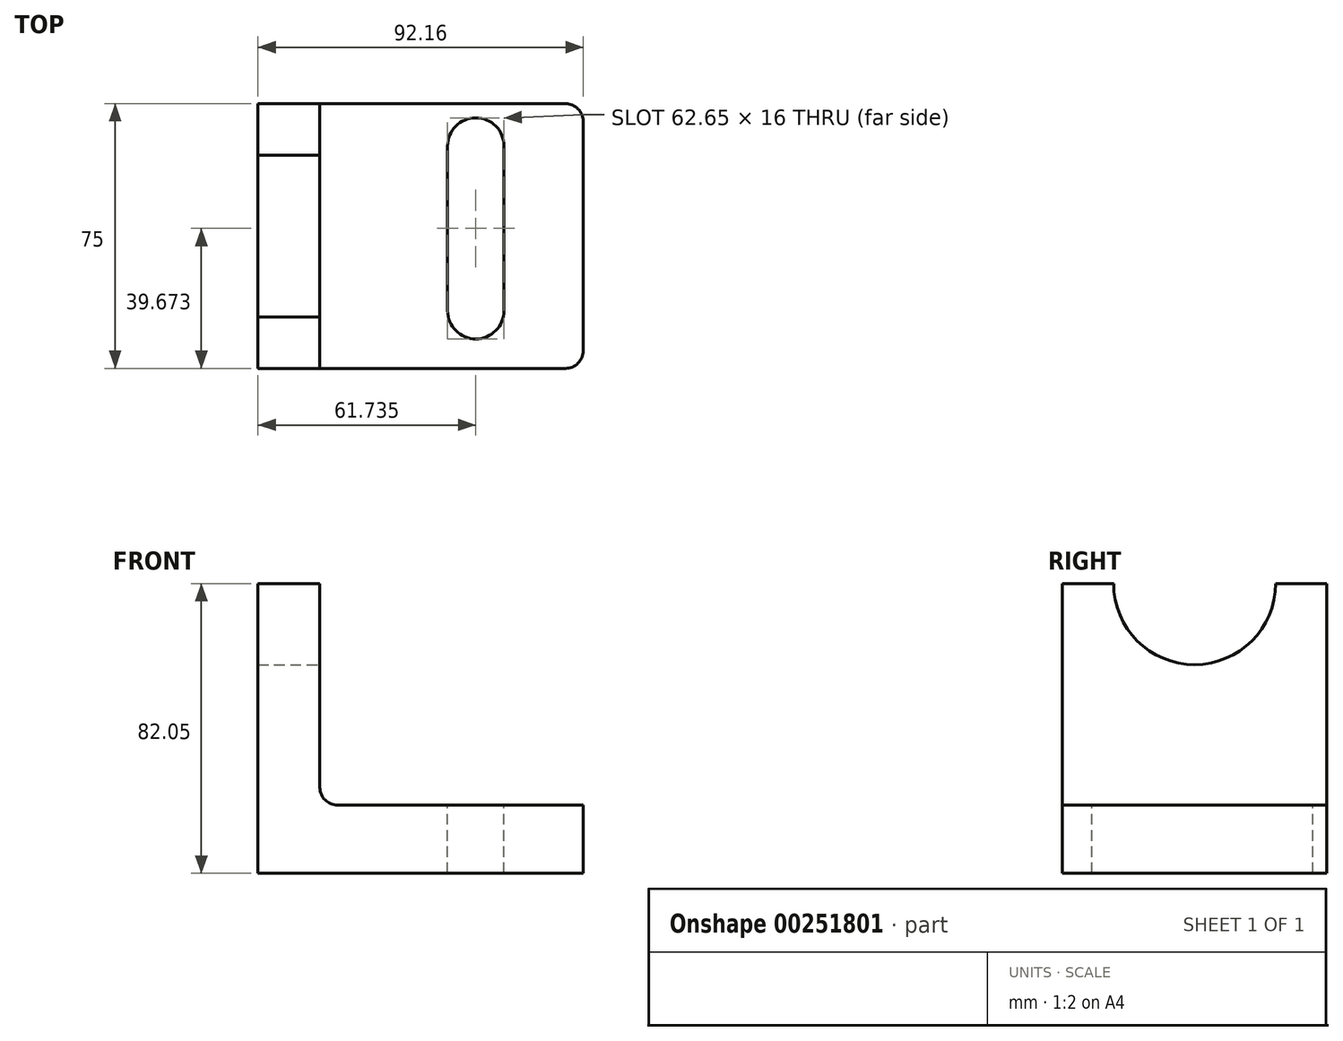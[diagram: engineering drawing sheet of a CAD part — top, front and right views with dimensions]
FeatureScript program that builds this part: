
annotation { "Feature Type Name" : "Feature", "Feature Type Description" : "" }
export const myFeature = defineFeature(function(context is Context, id is Id, definition is map)
    precondition{}
    {
        {
            var Q0;
            Q0=qCreatedBy(makeId("Front.planeOp"),FACE);
            var sketch = newSketch(context, id + "F0", { "sketchPlane" : qUnion([Q0])});
            skLineSegment(sketch, "E0.bottom", {"start": v(46.08, -9.65) * mm, "end": v(-46.08, -9.65) * mm});
            skLineSegment(sketch, "E0.top", {"start": v(46.08, 9.65) * mm, "end": v(-46.08, 9.65) * mm});
            skLineSegment(sketch, "E0.left", {"start": v(46.08, -9.65) * mm, "end": v(46.08, 9.65) * mm});
            skLineSegment(sketch, "E0.right", {"start": v(-46.08, -9.65) * mm, "end": v(-46.08, 9.65) * mm});
            skPoint(sketch, "E0.middle", {"position": v(0, 0) * mm});
            skLineSegment(sketch, "E1.bottom", {"start": v(-46.08, 9.65) * mm, "end": v(-28.52, 9.65) * mm});
            skLineSegment(sketch, "E1.top", {"start": v(-46.08, 72.4) * mm, "end": v(-28.52, 72.4) * mm});
            skLineSegment(sketch, "E1.left", {"start": v(-46.08, 9.65) * mm, "end": v(-46.08, 72.4) * mm});
            skLineSegment(sketch, "E1.right", {"start": v(-28.52, 9.65) * mm, "end": v(-28.52, 72.4) * mm});
            skSolve(sketch);
        }
        {
            var Q0;
            Q0 = qSketchRegion(id + "F0", true);
            extrude(context, id + "F1", {"entities" : qUnion([Q0]), "depth" : 75 * mm});
        }
        {
            var Q0;
            Q0=makeQuery(id+"F1.opExtrude","SWEPT_FACE",FACE,{"disambiguationData":[OSD([sQuery(id+"F0.wireOp",EDGE,"E1.right")])]});
            var sketch = newSketch(context, id + "F2", { "sketchPlane" : qUnion([Q0])});
            skCircle(sketch, "E2", {"center": v(-37.5, 72.4) * mm, "radius": 22.94 * mm});
            skSolve(sketch);
        }
        {
            var Q0;
            Q0 = qSketchRegion(id + "F2", true);
            extrude(context, id + "F3", {"entities" : qUnion([Q0]), "operationType" : NewBodyOperationType.REMOVE, "oppositeDirection" : true, "depth" : 25 * mm});
        }
        {
            var Q0;
            Q0=makeQuery(id+"F1.opExtrude","SWEPT_FACE",FACE,{"disambiguationData":[OSD([sQuery(id+"F0.wireOp",EDGE,"E0.top")])]});
            var sketch = newSketch(context, id + "F4", { "sketchPlane" : qUnion([Q0])});
            skArc(sketch, "E3", {"start": v(7.66, -58.65) * mm, "mid": v(15.66, -66.65) * mm, "end": v(23.66, -58.65) * mm});
            skArc(sketch, "E4", {"start": v(23.66, -12) * mm, "mid": v(15.66, -4) * mm, "end": v(7.66, -12) * mm});
            skLineSegment(sketch, "E5", {"start": v(7.66, -58.65) * mm, "end": v(7.66, -12) * mm});
            skLineSegment(sketch, "E6", {"start": v(23.66, -58.65) * mm, "end": v(23.66, -12) * mm});
            skSolve(sketch);
        }
        {
            var Q0;
            Q0 = qSketchRegion(id + "F4", true);
            extrude(context, id + "F5", {"entities" : qUnion([Q0]), "operationType" : NewBodyOperationType.REMOVE, "endBound" : BoundingType.THROUGH_ALL, "oppositeDirection" : true, "depth" : 25 * mm});
        }
        {
            var Q0;
            Q0=makeQuery(id+"F1.opExtrude","CAP_EDGE",EDGE,{"disambiguationData":[OSD([sQuery(id+"F0.wireOp",EDGE,"E0.left")])],"isStart":false});
            var Q1;
            Q1=makeQuery(id+"F1.opExtrude","CAP_EDGE",EDGE,{"disambiguationData":[OSD([sQuery(id+"F0.wireOp",EDGE,"E0.left")])],"isStart":true});
            fillet(context, id + "F6", {"entities" : qUnion([Q0, Q1]), "radius" : 5 * mm, "tangentPropagation" : true, "allowEdgeOverflow" : false});
        }
        {
            var Q0;
            Q0=makeQuery(id+"F1.opExtrude","SWEPT_EDGE",EDGE,{"disambiguationData":[OSD([sQuery(id+"F0.wireOp",EDGE,"E0.top"),sQuery(id+"F0.wireOp",EDGE,"E1.bottom"),sQuery(id+"F0.wireOp",EDGE,"E1.right")])]});
            fillet(context, id + "F7", {"entities" : qUnion([Q0]), "radius" : 5 * mm, "tangentPropagation" : true, "allowEdgeOverflow" : false});
        }
    });
